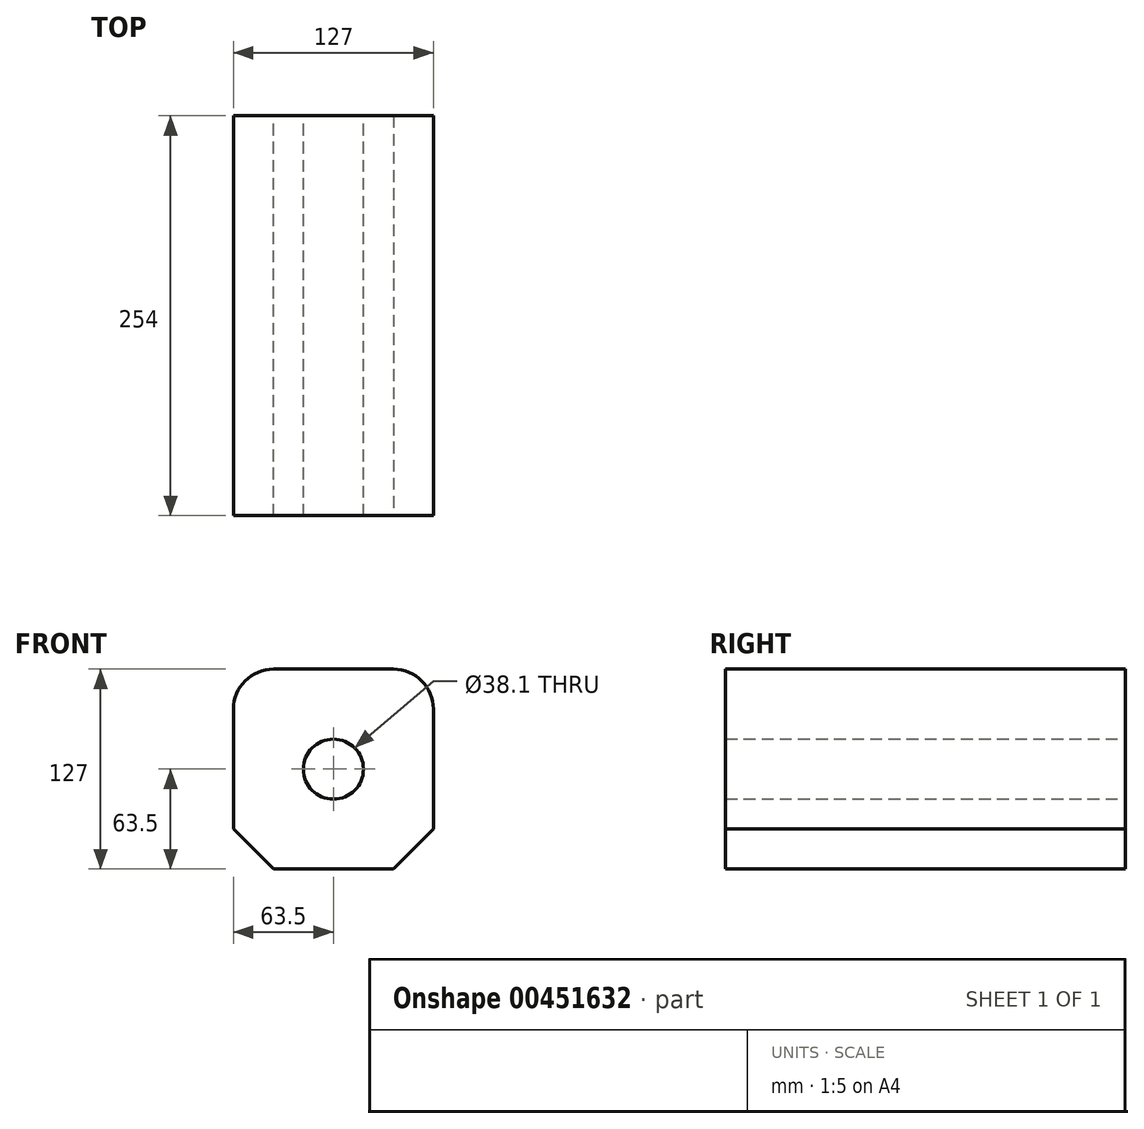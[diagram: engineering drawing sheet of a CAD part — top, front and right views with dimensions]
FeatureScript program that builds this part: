
annotation { "Feature Type Name" : "Feature", "Feature Type Description" : "" }
export const myFeature = defineFeature(function(context is Context, id is Id, definition is map)
    precondition{}
    {
        {
            var Q0;
            Q0=qCreatedBy(makeId("Front.planeOp"),FACE);
            var sketch = newSketch(context, id + "F0", { "sketchPlane" : qUnion([Q0])});
            skLineSegment(sketch, "E0.bottom", {"start": v(0, 0) * mm, "end": v(127, 0) * mm});
            skLineSegment(sketch, "E0.top", {"start": v(0, -127) * mm, "end": v(127, -127) * mm});
            skLineSegment(sketch, "E0.left", {"start": v(0, 0) * mm, "end": v(0, -127) * mm});
            skLineSegment(sketch, "E0.right", {"start": v(127, 0) * mm, "end": v(127, -127) * mm});
            skSolve(sketch);
        }
        {
            var Q0;
            Q0=qSketchRegion(id+"F0",true);
            extrude(context, id + "F1", {"entities" : qUnion([Q0]), "depth" : 254 * mm});
        }
        {
            var Q0;
            Q0=qCreatedBy(makeId("Front.planeOp"),FACE);
            var sketch = newSketch(context, id + "F2", { "sketchPlane" : qUnion([Q0])});
            skCircle(sketch, "E1", {"center": v(63.5, -63.5) * mm, "radius": 31.75 * mm});
            skSolve(sketch);
        }
        {
            var Q0;
            Q0=sQuery(id+"F2.wireOp",VERTEX,"E1.center");
            var Q1;
            Q1=makeQuery(id+"F1.opExtrude","SWEPT_BODY",BODY,{"disambiguationData":[OSD([sQuery(id+"F0.wireOp",EDGE,"E0.bottom"),sQuery(id+"F0.wireOp",EDGE,"E0.top"),sQuery(id+"F0.wireOp",EDGE,"E0.left"),sQuery(id+"F0.wireOp",EDGE,"E0.right")])]});
            hole(context, id + "F3", {"style" : HoleStyle.SIMPLE, "endStyle" : HoleEndStyle.THROUGH, "oppositeDirection" : true, "holeDiameter" : 38.1 * mm, "isTappedThrough" : true, "tappedDepth" : 12.7 * mm, "tapClearance" : 3, "locations" : qUnion([Q0]), "scope" : qUnion([Q1])});
        }
        {
            var Q0;
            Q0=makeQuery(id+"F1.opExtrude","SWEPT_EDGE",EDGE,{"disambiguationData":[OSD([sQuery(id+"F0.wireOp",EDGE,"E0.bottom"),sQuery(id+"F0.wireOp",EDGE,"E0.right")])]});
            var Q1;
            Q1=makeQuery(id+"F1.opExtrude","SWEPT_EDGE",EDGE,{"disambiguationData":[OSD([sQuery(id+"F0.wireOp",EDGE,"E0.bottom"),sQuery(id+"F0.wireOp",EDGE,"E0.left")])]});
            fillet(context, id + "F4", {"entities" : qUnion([Q0, Q1]), "radius" : 25.4 * mm, "tangentPropagation" : true, "allowEdgeOverflow" : false});
        }
        {
            var Q0;
            Q0=makeQuery(id+"F1.opExtrude","SWEPT_EDGE",EDGE,{"disambiguationData":[OSD([sQuery(id+"F0.wireOp",EDGE,"E0.top"),sQuery(id+"F0.wireOp",EDGE,"E0.right")])]});
            var Q1;
            Q1=makeQuery(id+"F1.opExtrude","SWEPT_EDGE",EDGE,{"disambiguationData":[OSD([sQuery(id+"F0.wireOp",EDGE,"E0.top"),sQuery(id+"F0.wireOp",EDGE,"E0.left")])]});
            chamfer(context, id + "F5", {"entities" : qUnion([Q0, Q1]), "width" : 25.4 * mm, "tangentPropagation" : true});
        }
    });
